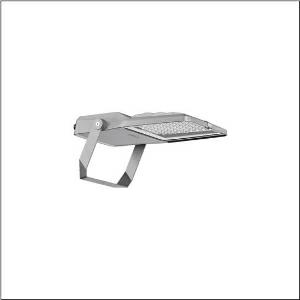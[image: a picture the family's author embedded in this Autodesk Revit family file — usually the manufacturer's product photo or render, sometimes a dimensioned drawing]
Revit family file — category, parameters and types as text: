
# Revit family: floodlight_fl_21_mini___rs12_5xa7771b2b1a_4199
name_source: partatom
category: Lighting Fixtures
units: mm (PartAtom-declared; Revit-internal decimal feet)

## family parameters
Cut with Voids When Loaded = No
Host = Face
Light Source = No
Part Type = Normal
Room Calculation Point = No
Round Connector Dimension = Use Diameter
Shared = No

## types (1)
- --- (1 x LED, 6300 lm, 45.5 W, 3000K)
    Apparent Load = 46 VA
    CIE Flux Codes = 79 92 99 100 100
    Color Rendering = 70
    Color Temperature = 3000K
    Default Elevation = 1800 mm
    Description = Floodlight FL 21 mini, floodlight, primary light control with lens, of PMMA, primary optical cover: protective disc, of toughened safety glass, transparent, light distribution: RS12, light emission: direct distribution, installation type: surface-mounted, LED, High Power LED, rated luminous flux: 6.300lm, luminous efficacy: 138lm/W, light colour: 730, colour temperature: 3000K, control gear: ECG iQ, control: Auto-Match, Temp-Guard, Lumen-Switch, Night-Set, Smart-Wire, Light-Fading, Desk-Remote (wireless, voltage-free reading and setting of iQ features in the workshop via application-optimized NFC function/RFID function), optimised constant luminous flux control (CLO 2.0), with terminal, 6-pole, mains connection: 220..240V, AC, 50/60Hz, start of lifetime: 46W, end of lifetime: 48W, reduction: 22W, luminaire housing, of diecast aluminium, powder-coated, Siteco® metallic grey (DB 702S), corrosivity category C5 according to DIN EN ISO 12944, mounting bracket, of steel, galvanised, powder-coated, Siteco® metallic grey (DB 702S), protection rating (complete): IP66, insulation class (complete): insulation class II (safety insulation), certification: CE, ENEC, VDE, protection symbol: D, impact resistance: IK08, permissible operating ambient temperature: -40..+40°C, permissible operating ambient temperature for outdoor applications: -40..+50°C, standard: DIN EN 12944, packaging unit: 1 piece

Light Distribution: RS12
    Height = 70 mm
    Lamp = 1 x LED
    Lamp Light Flux = 6300 lm
    Lamp Power = 45.5 W
    Lamp count = 1
    Length = 485 mm
    Luminous efficacy = 138 lm/W
    Manufacturer = Siteco
    ModVariant = No
    Model = 5XA7771B2B1A
    Number of Poles = 1
    OnlyDefault = Yes
    Power Factor = 1
    Product Name = Floodlight FL 21 mini | RS12
    Product group = floodlight | pylon top
    ProductGroupID = 6101
    Protection Class = Protection class II
    Protection Degree = IP 66
    RLX_Detail_Level = 1
    RlxData = <blob elided: 90773 chars, md5=dc4cd34b>
    Socket = socket
    Standby Power = 0 W
    System Light Flux = 6300 lm
    System Power = 46 W
    Type Comments = factory setting: luminous flux: 100 % | dim-lin: 254 | 463 mA
    Type Image = l_1006845.jpg
    URL = http://relux.com
    VarID = @adj_079063
    Voltage = 0 V
    Weight = 0.00 kg
    Width = 337 mm

## geometry (parser evidence)
native form markers: Blend x4, Sweep x14
no freeform markers — native parametric forms only
